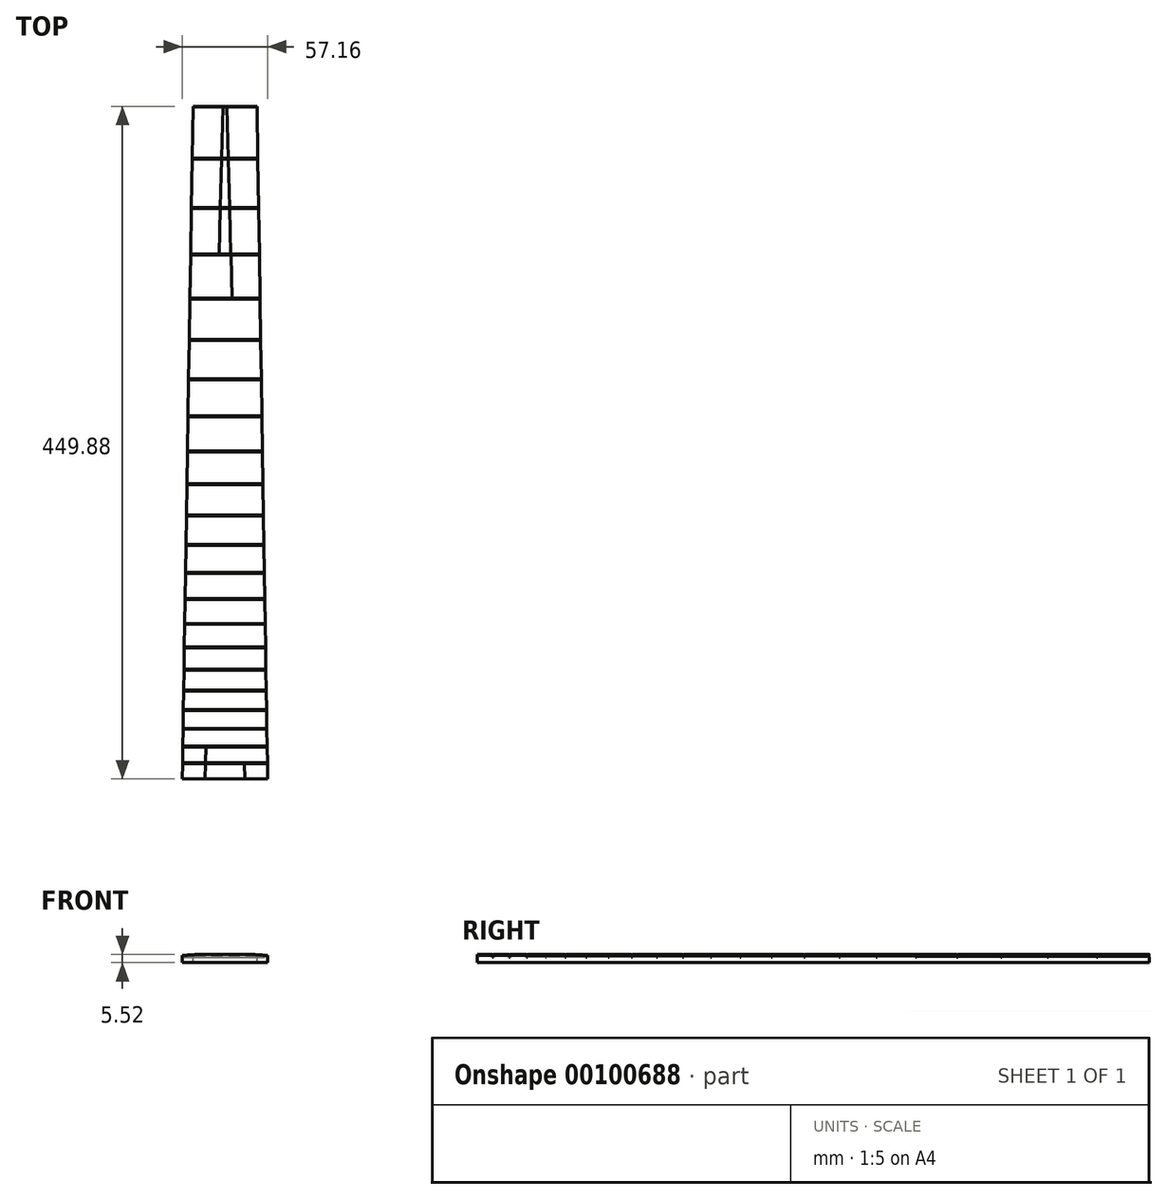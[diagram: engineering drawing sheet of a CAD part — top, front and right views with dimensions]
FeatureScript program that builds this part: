
annotation { "Feature Type Name" : "Feature", "Feature Type Description" : "" }
export const myFeature = defineFeature(function(context is Context, id is Id, definition is map)
    precondition{}
    {
        {
            var Q0;
            Q0=qCreatedBy(makeId("Front.planeOp"),FACE);
            var sketch = newSketch(context, id + "F0", { "sketchPlane" : qUnion([Q0])});
            skLineSegment(sketch, "E0.bottom", {"start": v(-28.57, 4.76) * mm, "end": v(28.57, 4.76) * mm, "construction": true});
            skLineSegment(sketch, "E0.top", {"start": v(-28.57, 0) * mm, "end": v(28.57, 0) * mm});
            skLineSegment(sketch, "E0.left", {"start": v(-28.57, 4.76) * mm, "end": v(-28.57, 0) * mm});
            skLineSegment(sketch, "E0.right", {"start": v(28.58, 4.76) * mm, "end": v(28.58, 0) * mm});
            skLineSegment(sketch, "E1", {"start": v(0, 0) * mm, "end": v(0, 5.52) * mm, "construction": true});
            skArc(sketch, "E2", {"start": v(-13.35, 5.52) * mm, "mid": v(-20.97, 5.33) * mm, "end": v(-28.58, 4.76) * mm});
            skLineSegment(sketch, "E3", {"start": v(-13.35, 5.52) * mm, "end": v(13.35, 5.52) * mm});
            skPoint(sketch, "E4.orphan", {"position": v(-16.25, 5.52) * mm});
            skPoint(sketch, "E5.orphan", {"position": v(16.25, 5.52) * mm});
            skArc(sketch, "E6.trimOffspring", {"start": v(13.35, 5.52) * mm, "mid": v(20.97, 5.33) * mm, "end": v(28.57, 4.76) * mm});
            skSolve(sketch);
        }
        {
            var Q0;
            Q0=qCreatedBy(makeId("Front.planeOp"),FACE);
            cPlane(context, id + "F1", {"entities" : qUnion([Q0]), "cplaneType" : CPlaneType.OFFSET, "offset" : 449.88 * mm, "oppositeDirection" : true, "width" : 150 * mm, "height" : 150 * mm});
        }
        {
            var Q0;
            Q0=qCreatedBy(id+"F1.planeOp",FACE);
            var sketch = newSketch(context, id + "F2", { "sketchPlane" : qUnion([Q0])});
            skLineSegment(sketch, "E7.bottom", {"start": v(21.43, 0) * mm, "end": v(-21.43, 0) * mm});
            skLineSegment(sketch, "E7.top", {"start": v(21.43, 4.2) * mm, "end": v(-21.43, 4.2) * mm, "construction": true});
            skLineSegment(sketch, "E7.left", {"start": v(21.43, 0) * mm, "end": v(21.43, 4.2) * mm});
            skLineSegment(sketch, "E7.right", {"start": v(-21.43, 0) * mm, "end": v(-21.43, 4.2) * mm});
            skLineSegment(sketch, "E8", {"start": v(0, 0) * mm, "end": v(0, 5.52) * mm, "construction": true});
            skPoint(sketch, "E8.endSnap0", {"position": v(0, 4.2) * mm});
            skArc(sketch, "E9", {"start": v(21.43, 4.2) * mm, "mid": v(11.4, 5.2) * mm, "end": v(1.31, 5.52) * mm});
            skLineSegment(sketch, "E10", {"start": v(1.31, 5.52) * mm, "end": v(-1.31, 5.52) * mm});
            skPoint(sketch, "E11.orphan", {"position": v(19.15, 5.52) * mm});
            skArc(sketch, "E12.MirrorCS", {"start": v(-21.43, 4.2) * mm, "mid": v(-11.4, 5.2) * mm, "end": v(-1.31, 5.52) * mm});
            skPoint(sketch, "E13.orphan", {"position": v(-19.15, 5.52) * mm});
            skSolve(sketch);
        }
        {
            var Q0;
            Q0=makeQuery(id+"F0.imprint","IMPRINT",FACE,{"disambiguationData":[TD([[makeQuery(id+"F0.imprint","IMPRINT",EDGE,{"derivedFrom":sQuery(id+"F0.wireOp",EDGE,"E0.top")}),1.0]])]});
            var Q1;
            Q1=makeQuery(id+"F2.imprint","IMPRINT",FACE,{"disambiguationData":[TD([[makeQuery(id+"F2.imprint","IMPRINT",EDGE,{"derivedFrom":sQuery(id+"F2.wireOp",EDGE,"E7.bottom")}),-1.0]])]});
            loft(context, id + "F3", {"sheetProfilesArray" : [{ "sheetProfileEntities" : qUnion([Q0]) }, { "sheetProfileEntities" : qUnion([Q1]) }]});
        }
        {
            var Q0;
            Q0=qCreatedBy(makeId("Right.planeOp"),FACE);
            var sketch = newSketch(context, id + "F4", { "sketchPlane" : qUnion([Q0])});
            skLineSegment(sketch, "E14", {"start": v(0, 0) * mm, "end": v(449.88, 0) * mm, "construction": true});
            skLineSegment(sketch, "E15", {"start": v(0, 0) * mm, "end": v(0, 5.52) * mm, "construction": true});
            skLineSegment(sketch, "E16", {"start": v(449.88, 0) * mm, "end": v(449.88, 4) * mm, "construction": true});
            skLineSegment(sketch, "E17", {"start": v(449.88, 5.52) * mm, "end": v(414.96, 5.52) * mm, "construction": true});
            skLineSegment(sketch, "E18", {"start": v(414.96, 5.52) * mm, "end": v(381.97, 5.52) * mm, "construction": true});
            skLineSegment(sketch, "E19", {"start": v(381.97, 5.52) * mm, "end": v(350.82, 5.52) * mm, "construction": true});
            skLineSegment(sketch, "E20", {"start": v(350.82, 5.52) * mm, "end": v(321.41, 5.52) * mm, "construction": true});
            skLineSegment(sketch, "E21", {"start": v(321.41, 5.52) * mm, "end": v(293.62, 5.52) * mm, "construction": true});
            skLineSegment(sketch, "E22", {"start": v(293.62, 5.52) * mm, "end": v(267.36, 5.52) * mm, "construction": true});
            skLineSegment(sketch, "E23", {"start": v(267.36, 5.52) * mm, "end": v(242.6, 5.52) * mm, "construction": true});
            skLineSegment(sketch, "E24", {"start": v(242.6, 5.52) * mm, "end": v(219.18, 5.52) * mm, "construction": true});
            skLineSegment(sketch, "E25", {"start": v(219.18, 5.52) * mm, "end": v(197.08, 5.52) * mm, "construction": true});
            skLineSegment(sketch, "E26", {"start": v(197.08, 5.52) * mm, "end": v(176.2, 5.52) * mm, "construction": true});
            skLineSegment(sketch, "E27", {"start": v(176.2, 5.52) * mm, "end": v(156.46, 5.52) * mm, "construction": true});
            skLineSegment(sketch, "E28", {"start": v(156.46, 5.52) * mm, "end": v(137.85, 5.52) * mm, "construction": true});
            skLineSegment(sketch, "E29", {"start": v(137.85, 5.52) * mm, "end": v(120.24, 5.52) * mm, "construction": true});
            skLineSegment(sketch, "E30", {"start": v(120.24, 5.52) * mm, "end": v(103.63, 5.52) * mm, "construction": true});
            skLineSegment(sketch, "E31", {"start": v(103.63, 5.52) * mm, "end": v(87.96, 5.52) * mm, "construction": true});
            skLineSegment(sketch, "E32", {"start": v(87.96, 5.52) * mm, "end": v(73.13, 5.52) * mm, "construction": true});
            skLineSegment(sketch, "E33", {"start": v(73.13, 5.52) * mm, "end": v(59.13, 5.52) * mm, "construction": true});
            skLineSegment(sketch, "E34", {"start": v(59.13, 5.52) * mm, "end": v(45.92, 5.52) * mm, "construction": true});
            skLineSegment(sketch, "E35", {"start": v(45.92, 5.52) * mm, "end": v(33.45, 5.52) * mm, "construction": true});
            skLineSegment(sketch, "E36", {"start": v(33.45, 5.52) * mm, "end": v(21.64, 5.52) * mm, "construction": true});
            skLineSegment(sketch, "E37", {"start": v(21.64, 5.52) * mm, "end": v(10.52, 5.52) * mm, "construction": true});
            skLineSegment(sketch, "E38", {"start": v(10.52, 5.52) * mm, "end": v(0, 5.52) * mm, "construction": true});
            skLineSegment(sketch, "E39.bottom", {"start": v(10.8, 3.52) * mm, "end": v(10.22, 3.52) * mm});
            skLineSegment(sketch, "E39.top", {"start": v(10.8, 7.52) * mm, "end": v(10.22, 7.52) * mm});
            skLineSegment(sketch, "E39.left", {"start": v(10.8, 3.52) * mm, "end": v(10.8, 7.52) * mm});
            skLineSegment(sketch, "E39.right", {"start": v(10.22, 3.52) * mm, "end": v(10.22, 7.52) * mm});
            skPoint(sketch, "E39.middle", {"position": v(10.52, 5.52) * mm});
            skLineSegment(sketch, "E40.bottom", {"start": v(21.93, 3.52) * mm, "end": v(21.35, 3.52) * mm});
            skLineSegment(sketch, "E40.top", {"start": v(21.93, 7.52) * mm, "end": v(21.35, 7.52) * mm});
            skLineSegment(sketch, "E40.left", {"start": v(21.93, 3.52) * mm, "end": v(21.93, 7.52) * mm});
            skLineSegment(sketch, "E40.right", {"start": v(21.35, 3.52) * mm, "end": v(21.35, 7.52) * mm});
            skPoint(sketch, "E40.middle", {"position": v(21.64, 5.52) * mm});
            skLineSegment(sketch, "E41.bottom", {"start": v(33.74, 3.52) * mm, "end": v(33.16, 3.52) * mm});
            skLineSegment(sketch, "E41.top", {"start": v(33.74, 7.52) * mm, "end": v(33.16, 7.52) * mm});
            skLineSegment(sketch, "E41.left", {"start": v(33.74, 3.52) * mm, "end": v(33.74, 7.52) * mm});
            skLineSegment(sketch, "E41.right", {"start": v(33.16, 3.52) * mm, "end": v(33.16, 7.52) * mm});
            skPoint(sketch, "E41.middle", {"position": v(33.45, 5.52) * mm});
            skLineSegment(sketch, "E42.bottom", {"start": v(45.63, 7.52) * mm, "end": v(46.22, 7.52) * mm});
            skLineSegment(sketch, "E42.top", {"start": v(45.63, 3.52) * mm, "end": v(46.22, 3.52) * mm});
            skLineSegment(sketch, "E42.left", {"start": v(45.63, 7.52) * mm, "end": v(45.63, 3.52) * mm});
            skLineSegment(sketch, "E42.right", {"start": v(46.22, 7.52) * mm, "end": v(46.22, 3.52) * mm});
            skPoint(sketch, "E42.middle", {"position": v(45.92, 5.52) * mm});
            skLineSegment(sketch, "E43.bottom", {"start": v(58.84, 3.52) * mm, "end": v(59.42, 3.52) * mm});
            skLineSegment(sketch, "E43.top", {"start": v(58.84, 7.52) * mm, "end": v(59.42, 7.52) * mm});
            skLineSegment(sketch, "E43.left", {"start": v(58.84, 3.52) * mm, "end": v(58.84, 7.52) * mm});
            skLineSegment(sketch, "E43.right", {"start": v(59.42, 3.52) * mm, "end": v(59.42, 7.52) * mm});
            skPoint(sketch, "E43.middle", {"position": v(59.13, 5.52) * mm});
            skLineSegment(sketch, "E44.bottom", {"start": v(72.83, 7.52) * mm, "end": v(73.42, 7.52) * mm});
            skLineSegment(sketch, "E44.top", {"start": v(72.83, 3.52) * mm, "end": v(73.42, 3.52) * mm});
            skLineSegment(sketch, "E44.left", {"start": v(72.83, 7.52) * mm, "end": v(72.83, 3.52) * mm});
            skLineSegment(sketch, "E44.right", {"start": v(73.42, 7.52) * mm, "end": v(73.42, 3.52) * mm});
            skPoint(sketch, "E44.middle", {"position": v(73.13, 5.52) * mm});
            skLineSegment(sketch, "E45.bottom", {"start": v(88.25, 3.52) * mm, "end": v(87.67, 3.52) * mm});
            skLineSegment(sketch, "E45.top", {"start": v(88.25, 7.52) * mm, "end": v(87.67, 7.52) * mm});
            skLineSegment(sketch, "E45.left", {"start": v(88.25, 3.52) * mm, "end": v(88.25, 7.52) * mm});
            skLineSegment(sketch, "E45.right", {"start": v(87.67, 3.52) * mm, "end": v(87.67, 7.52) * mm});
            skPoint(sketch, "E45.middle", {"position": v(87.96, 5.52) * mm});
            skLineSegment(sketch, "E46.bottom", {"start": v(103.34, 3.52) * mm, "end": v(103.92, 3.52) * mm});
            skLineSegment(sketch, "E46.top", {"start": v(103.34, 7.52) * mm, "end": v(103.92, 7.52) * mm});
            skLineSegment(sketch, "E46.left", {"start": v(103.34, 3.52) * mm, "end": v(103.34, 7.52) * mm});
            skLineSegment(sketch, "E46.right", {"start": v(103.92, 3.52) * mm, "end": v(103.92, 7.52) * mm});
            skPoint(sketch, "E46.middle", {"position": v(103.63, 5.52) * mm});
            skLineSegment(sketch, "E47.bottom", {"start": v(119.95, 3.52) * mm, "end": v(120.54, 3.52) * mm});
            skLineSegment(sketch, "E47.top", {"start": v(119.95, 7.52) * mm, "end": v(120.54, 7.52) * mm});
            skLineSegment(sketch, "E47.left", {"start": v(119.95, 3.52) * mm, "end": v(119.95, 7.52) * mm});
            skLineSegment(sketch, "E47.right", {"start": v(120.54, 3.52) * mm, "end": v(120.54, 7.52) * mm});
            skPoint(sketch, "E47.middle", {"position": v(120.24, 5.52) * mm});
            skLineSegment(sketch, "E48.bottom", {"start": v(137.55, 3.52) * mm, "end": v(138.14, 3.52) * mm});
            skLineSegment(sketch, "E48.top", {"start": v(137.55, 7.52) * mm, "end": v(138.14, 7.52) * mm});
            skLineSegment(sketch, "E48.left", {"start": v(137.55, 3.52) * mm, "end": v(137.55, 7.52) * mm});
            skLineSegment(sketch, "E48.right", {"start": v(138.14, 3.52) * mm, "end": v(138.14, 7.52) * mm});
            skPoint(sketch, "E48.middle", {"position": v(137.85, 5.52) * mm});
            skLineSegment(sketch, "E49.bottom", {"start": v(156.17, 3.52) * mm, "end": v(156.76, 3.52) * mm});
            skLineSegment(sketch, "E49.top", {"start": v(156.17, 7.52) * mm, "end": v(156.76, 7.52) * mm});
            skLineSegment(sketch, "E49.left", {"start": v(156.17, 3.52) * mm, "end": v(156.17, 7.52) * mm});
            skLineSegment(sketch, "E49.right", {"start": v(156.76, 3.52) * mm, "end": v(156.76, 7.52) * mm});
            skPoint(sketch, "E49.middle", {"position": v(156.46, 5.52) * mm});
            skLineSegment(sketch, "E50.bottom", {"start": v(175.9, 3.52) * mm, "end": v(176.5, 3.52) * mm});
            skLineSegment(sketch, "E50.top", {"start": v(175.9, 7.52) * mm, "end": v(176.5, 7.52) * mm});
            skLineSegment(sketch, "E50.left", {"start": v(175.9, 3.52) * mm, "end": v(175.9, 7.52) * mm});
            skLineSegment(sketch, "E50.right", {"start": v(176.5, 3.52) * mm, "end": v(176.5, 7.52) * mm});
            skPoint(sketch, "E50.middle", {"position": v(176.2, 5.52) * mm});
            skLineSegment(sketch, "E51.bottom", {"start": v(196.79, 3.52) * mm, "end": v(197.37, 3.52) * mm});
            skLineSegment(sketch, "E51.top", {"start": v(196.79, 7.52) * mm, "end": v(197.37, 7.52) * mm});
            skLineSegment(sketch, "E51.left", {"start": v(196.79, 3.52) * mm, "end": v(196.79, 7.52) * mm});
            skLineSegment(sketch, "E51.right", {"start": v(197.37, 3.52) * mm, "end": v(197.37, 7.52) * mm});
            skPoint(sketch, "E51.middle", {"position": v(197.08, 5.52) * mm});
            skLineSegment(sketch, "E52.bottom", {"start": v(219.47, 3.52) * mm, "end": v(218.88, 3.52) * mm});
            skLineSegment(sketch, "E52.top", {"start": v(219.47, 7.52) * mm, "end": v(218.88, 7.52) * mm});
            skLineSegment(sketch, "E52.left", {"start": v(219.47, 3.52) * mm, "end": v(219.47, 7.52) * mm});
            skLineSegment(sketch, "E52.right", {"start": v(218.88, 3.52) * mm, "end": v(218.88, 7.52) * mm});
            skPoint(sketch, "E52.middle", {"position": v(219.18, 5.52) * mm});
            skLineSegment(sketch, "E53.bottom", {"start": v(242.89, 3.52) * mm, "end": v(242.3, 3.52) * mm});
            skLineSegment(sketch, "E53.top", {"start": v(242.89, 7.52) * mm, "end": v(242.3, 7.52) * mm});
            skLineSegment(sketch, "E53.left", {"start": v(242.89, 3.52) * mm, "end": v(242.89, 7.52) * mm});
            skLineSegment(sketch, "E53.right", {"start": v(242.3, 3.52) * mm, "end": v(242.3, 7.52) * mm});
            skPoint(sketch, "E53.middle", {"position": v(242.6, 5.52) * mm});
            skLineSegment(sketch, "E54.bottom", {"start": v(267.65, 3.52) * mm, "end": v(267.07, 3.52) * mm});
            skLineSegment(sketch, "E54.top", {"start": v(267.65, 7.52) * mm, "end": v(267.07, 7.52) * mm});
            skLineSegment(sketch, "E54.left", {"start": v(267.65, 3.52) * mm, "end": v(267.65, 7.52) * mm});
            skLineSegment(sketch, "E54.right", {"start": v(267.07, 3.52) * mm, "end": v(267.07, 7.52) * mm});
            skPoint(sketch, "E54.middle", {"position": v(267.36, 5.52) * mm});
            skLineSegment(sketch, "E55.bottom", {"start": v(293.92, 3.52) * mm, "end": v(293.33, 3.52) * mm});
            skLineSegment(sketch, "E55.top", {"start": v(293.92, 7.52) * mm, "end": v(293.33, 7.52) * mm});
            skLineSegment(sketch, "E55.left", {"start": v(293.92, 3.52) * mm, "end": v(293.92, 7.52) * mm});
            skLineSegment(sketch, "E55.right", {"start": v(293.33, 3.52) * mm, "end": v(293.33, 7.52) * mm});
            skPoint(sketch, "E55.middle", {"position": v(293.62, 5.52) * mm});
            skLineSegment(sketch, "E56.bottom", {"start": v(321.7, 3.52) * mm, "end": v(321.12, 3.52) * mm});
            skLineSegment(sketch, "E56.top", {"start": v(321.7, 7.52) * mm, "end": v(321.12, 7.52) * mm});
            skLineSegment(sketch, "E56.left", {"start": v(321.7, 3.52) * mm, "end": v(321.7, 7.52) * mm});
            skLineSegment(sketch, "E56.right", {"start": v(321.12, 3.52) * mm, "end": v(321.12, 7.52) * mm});
            skPoint(sketch, "E56.middle", {"position": v(321.41, 5.52) * mm});
            skLineSegment(sketch, "E57.bottom", {"start": v(351.12, 3.52) * mm, "end": v(350.53, 3.52) * mm});
            skLineSegment(sketch, "E57.top", {"start": v(351.12, 7.52) * mm, "end": v(350.53, 7.52) * mm});
            skLineSegment(sketch, "E57.left", {"start": v(351.12, 3.52) * mm, "end": v(351.12, 7.52) * mm});
            skLineSegment(sketch, "E57.right", {"start": v(350.53, 3.52) * mm, "end": v(350.53, 7.52) * mm});
            skPoint(sketch, "E57.middle", {"position": v(350.82, 5.52) * mm});
            skLineSegment(sketch, "E58.bottom", {"start": v(382.26, 3.52) * mm, "end": v(381.67, 3.52) * mm});
            skLineSegment(sketch, "E58.top", {"start": v(382.26, 7.52) * mm, "end": v(381.67, 7.52) * mm});
            skLineSegment(sketch, "E58.left", {"start": v(382.26, 3.52) * mm, "end": v(382.26, 7.52) * mm});
            skLineSegment(sketch, "E58.right", {"start": v(381.67, 3.52) * mm, "end": v(381.67, 7.52) * mm});
            skPoint(sketch, "E58.middle", {"position": v(381.97, 5.52) * mm});
            skLineSegment(sketch, "E59.bottom", {"start": v(415.25, 3.52) * mm, "end": v(414.67, 3.52) * mm});
            skLineSegment(sketch, "E59.top", {"start": v(415.25, 7.52) * mm, "end": v(414.67, 7.52) * mm});
            skLineSegment(sketch, "E59.left", {"start": v(415.25, 3.52) * mm, "end": v(415.25, 7.52) * mm});
            skLineSegment(sketch, "E59.right", {"start": v(414.67, 3.52) * mm, "end": v(414.67, 7.52) * mm});
            skPoint(sketch, "E59.middle", {"position": v(414.96, 5.52) * mm});
            skPoint(sketch, "E60.middle", {"position": v(449.88, 4) * mm});
            skPoint(sketch, "E60.cornerSnap0", {"position": v(449.88, 2) * mm});
            skLineSegment(sketch, "E61.bottom", {"start": v(450.18, 3.52) * mm, "end": v(449.6, 3.52) * mm});
            skLineSegment(sketch, "E61.top", {"start": v(450.18, 7.52) * mm, "end": v(449.6, 7.52) * mm});
            skLineSegment(sketch, "E61.left", {"start": v(450.18, 3.52) * mm, "end": v(450.18, 7.52) * mm});
            skLineSegment(sketch, "E61.right", {"start": v(449.6, 3.52) * mm, "end": v(449.6, 7.52) * mm});
            skPoint(sketch, "E61.middle", {"position": v(449.88, 5.52) * mm});
            skSolve(sketch);
        }
        {
            var Q0;
            Q0 = qSketchRegion(id + "F4", true);
            extrude(context, id + "F5", {"entities" : qUnion([Q0]), "operationType" : NewBodyOperationType.REMOVE, "oppositeDirection" : true, "depth" : 60 * mm, "symmetric" : true});
        }
    });
